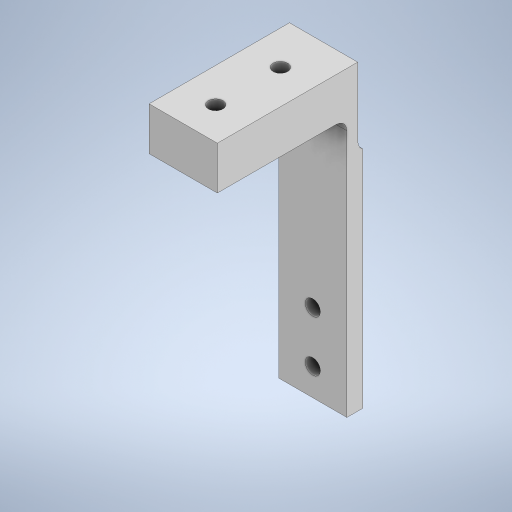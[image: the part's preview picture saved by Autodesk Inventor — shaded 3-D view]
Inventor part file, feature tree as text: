
AUTODESK INVENTOR PART (.ipt)
format: ipt  version: 2024.2 (Build 282272000, 272)  size: 606,720 bytes
history: native  units: in
note: dims shown in document units (in); Inventor stores cm internally (conversion verified against a paired STEP export)
features: extrude x5, sketch x5, projected_geometry x4, fillet x2, chamfer x1
ambient origin geometry x8: Origin, YZ Plane, XZ Plane, XY Plane, X Axis, Y Axis, Z Axis, Center Point
bodies: Solid1 (feature_tree)
feature tree (17):
  extrude  "Extrusion1"  Depth=3.5in
  extrude  "Extrusion2"  Depth=0.5in
  extrude  "Extrusion3"  Depth=1.5in
  extrude  "Extrusion4"  Depth=0.06in
  extrude  "Extrusion5"  Depth=0.125in
  fillet  "Fillet1"  Radius=0.1772in
  chamfer  "Chamfer1"  Distance=0.125in
  fillet  "Fillet2"  Radius=0.17in
  sketch  "Sketch1"  dims[d0=0.79in d1=3.5in]
  sketch  "Sketch2"  dims[d2=0.125in d3=0.0in d4=0.5in]
  sketch  "Sketch3"  dims[d5=1.5in d6=0.0in d7=0.9in]
  projected_geometry  "Projected Loop1"
  sketch  "Sketch4"  dims[d8=0.06in d9=0.0in d10=0.315in]
  projected_geometry  "Projected Loop2"
  projected_geometry  "Projected Loop3"
  sketch  "Sketch5"  dims[d11=0.5906in d12=0.1772in d13=0.1772in d14=0.125in d15=0.0in d16=0.17in d17=0.17in d18=0.375in d19=0.375in d20=0.0in d21=0.0in d22=0.125in d23=0.09in d24=0.125in d25=45.0deg d26=0.125in]
  projected_geometry  "Projected Loop4"
